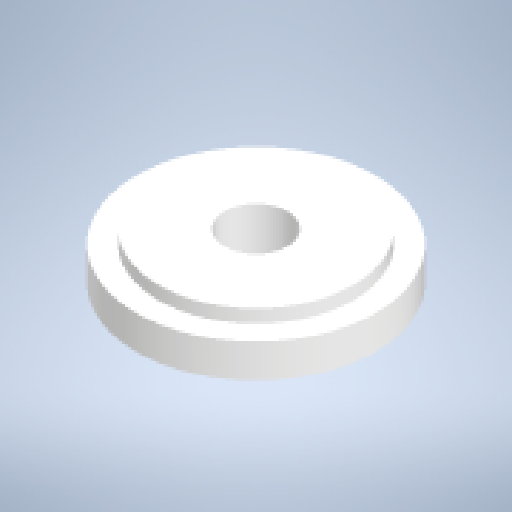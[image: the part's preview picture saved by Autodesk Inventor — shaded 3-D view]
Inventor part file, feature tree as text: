
AUTODESK INVENTOR PART (.ipt)
format: ipt  version: 2023 (Build 270158000, 158)  size: 155,648 bytes
history: native  units: in
note: dims shown in document units (in); Inventor stores cm internally (conversion verified against a paired STEP export)
features: revolve x1, sketch x1
ambient origin geometry x8: Origin, YZ Plane, XZ Plane, XY Plane, X Axis, Y Axis, Z Axis, Center Point
bodies: Solid1 (feature_tree)
feature tree (2):
  revolve  "Revolution1"  [1 undecoded]
  sketch  "Sketch1"  dims[d0=0.2756in d1=1.063in d2=0.0787in d3=0.0484in d4=0.1496in d5=0.7874in d6=360.0deg d7=0.8661in d8=0.0591in]
note: 1 required parameter value undecoded (feature->parameter linkage not recoverable at this tier; creation-order binding heuristic only, values carry confidence <= 0.55)
